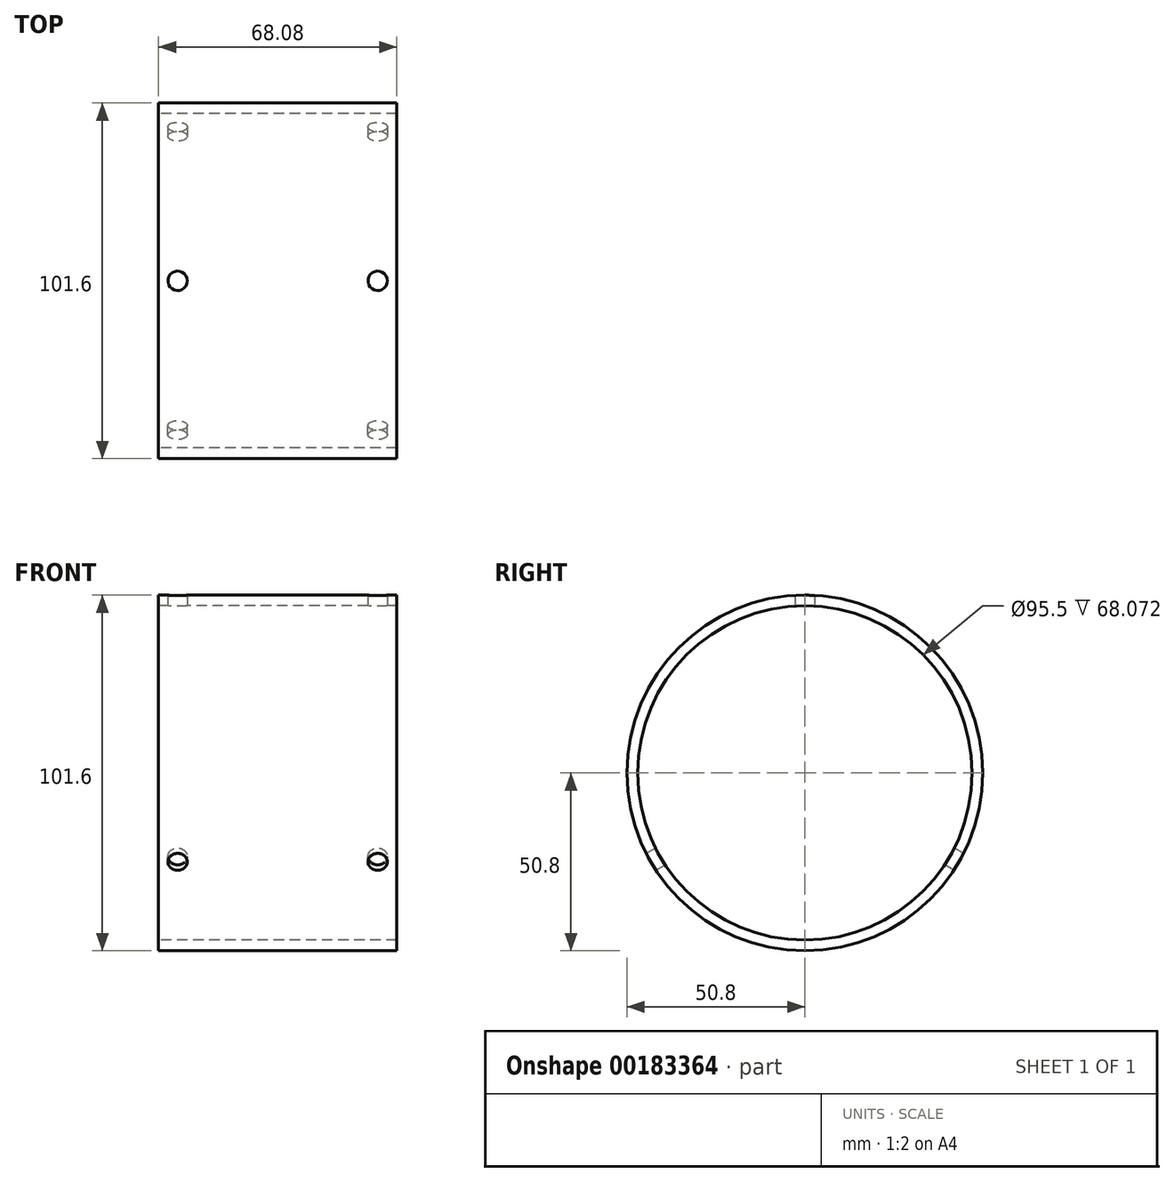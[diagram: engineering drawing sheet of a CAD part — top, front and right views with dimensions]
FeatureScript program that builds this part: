
annotation { "Feature Type Name" : "Feature", "Feature Type Description" : "" }
export const myFeature = defineFeature(function(context is Context, id is Id, definition is map)
    precondition{}
    {
        {
            var Q0;
            Q0=qCreatedBy(makeId("Right.planeOp"),FACE);
            var sketch = newSketch(context, id + "F0", { "sketchPlane" : qUnion([Q0])});
            skCircle(sketch, "E0", {"center": v(0, 0) * mm, "radius": 47.75 * mm});
            skCircle(sketch, "E1", {"center": v(0, 0) * mm, "radius": 50.8 * mm});
            skSolve(sketch);
        }
        {
            var Q0;
            Q0 = qSketchRegion(id + "F0", true);
            extrude(context, id + "F1", {"entities" : qUnion([Q0]), "endBound" : BoundingType.SYMMETRIC, "depth" : 68.07 * mm});
        }
        {
            var Q0;
            Q0=qCreatedBy(makeId("Top.planeOp"),FACE);
            cPlane(context, id + "F2", {"entities" : qUnion([Q0]), "cplaneType" : CPlaneType.OFFSET, "offset" : 50.8 * mm, "width" : 152.4 * mm, "height" : 152.4 * mm});
        }
        {
            var Q0;
            Q0=qCreatedBy(id+"F2.planeOp",FACE);
            var sketch = newSketch(context, id + "F3", { "sketchPlane" : qUnion([Q0])});
            skLineSegment(sketch, "E2.0", {"start": v(-34.04, 50.8) * mm, "end": v(-34.04, -50.8) * mm, "construction": true});
            skLineSegment(sketch, "E3.0", {"start": v(34.04, 50.8) * mm, "end": v(34.04, -50.8) * mm, "construction": true});
            skLineSegment(sketch, "E4", {"start": v(0, -101.71) * mm, "end": v(0, 113.33) * mm, "construction": true});
            skLineSegment(sketch, "E5", {"start": v(-71.88, 0) * mm, "end": v(58.67, 0) * mm, "construction": true});
            skPoint(sketch, "E5.endSnap0", {"position": v(34.04, 0) * mm});
            skLineSegment(sketch, "E6.0", {"start": v(-28.58, -101.71) * mm, "end": v(-28.58, 113.33) * mm, "construction": true});
            skPoint(sketch, "E7", {"position": v(-28.58, 0) * mm});
            skPoint(sketch, "E8.MirrorP", {"position": v(28.58, 0) * mm});
            skCircle(sketch, "E9", {"center": v(-28.58, 0) * mm, "radius": 2.78 * mm});
            skCircle(sketch, "E10", {"center": v(28.58, 0) * mm, "radius": 2.78 * mm});
            skSolve(sketch);
        }
        {
            var Q0;
            Q0 = qSketchRegion(id + "F3", true);
            extrude(context, id + "F4", {"entities" : qUnion([Q0]), "endBound" : BoundingType.SYMMETRIC, "depth" : 25.4 * mm});
        }
        {
            var Q0;
            Q0=qCreatedBy(makeId("Top.planeOp"),FACE);
            var sketch = newSketch(context, id + "F5", { "sketchPlane" : qUnion([Q0])});
            skLineSegment(sketch, "E11", {"start": v(-89.2, 0) * mm, "end": v(93.73, 0) * mm, "construction": true});
            skSolve(sketch);
        }
        {
            var Q0;
            Q0=makeQuery(id+"F4.opExtrude","SWEPT_BODY",BODY,{"disambiguationData":[OSD([sQuery(id+"F3.wireOp",EDGE,"E9")])]});
            var Q1;
            Q1=makeQuery(id+"F4.opExtrude","SWEPT_BODY",BODY,{"disambiguationData":[OSD([sQuery(id+"F3.wireOp",EDGE,"E10")])]});
            var Q2;
            Q2=sQuery(id+"F5.wireOp",EDGE,"E11");
            circularPattern(context, id + "F6", {"entities" : qUnion([Q0, Q1]), "axis" : qUnion([Q2]), "angle" : 120 * degree, "instanceCount" : 3});
        }
        {
            var Q0;
            Q0=makeQuery(id+"F4.opExtrude","SWEPT_BODY",BODY,{"disambiguationData":[OSD([sQuery(id+"F3.wireOp",EDGE,"E9")])]});
            var Q1;
            Q1=makeQuery(id+"F4.opExtrude","SWEPT_BODY",BODY,{"disambiguationData":[OSD([sQuery(id+"F3.wireOp",EDGE,"E10")])]});
            var Q2;
            Q2=makeQuery(id+"F6.opPattern","COPY",BODY,{"derivedFrom":makeQuery(id+"F4.opExtrude","SWEPT_BODY",BODY,{"disambiguationData":[OSD([sQuery(id+"F3.wireOp",EDGE,"E9")])]}),"instanceName":"2"});
            var Q3;
            Q3=makeQuery(id+"F6.opPattern","COPY",BODY,{"derivedFrom":makeQuery(id+"F4.opExtrude","SWEPT_BODY",BODY,{"disambiguationData":[OSD([sQuery(id+"F3.wireOp",EDGE,"E10")])]}),"instanceName":"2"});
            var Q4;
            Q4=makeQuery(id+"F6.opPattern","COPY",BODY,{"derivedFrom":makeQuery(id+"F4.opExtrude","SWEPT_BODY",BODY,{"disambiguationData":[OSD([sQuery(id+"F3.wireOp",EDGE,"E9")])]}),"instanceName":"1"});
            var Q5;
            Q5=makeQuery(id+"F6.opPattern","COPY",BODY,{"derivedFrom":makeQuery(id+"F4.opExtrude","SWEPT_BODY",BODY,{"disambiguationData":[OSD([sQuery(id+"F3.wireOp",EDGE,"E10")])]}),"instanceName":"1"});
            var Q6;
            Q6=makeQuery(id+"F1.opExtrude","SWEPT_BODY",BODY,{"disambiguationData":[OSD([sQuery(id+"F0.wireOp",EDGE,"E0"),sQuery(id+"F0.wireOp",EDGE,"E1")])]});
            booleanBodies(context, id + "F7", {"operationType" : BooleanOperationType.SUBTRACTION, "tools" : qUnion([Q0, Q1, Q2, Q3, Q4, Q5]), "targets" : qUnion([Q6])});
        }
    });
